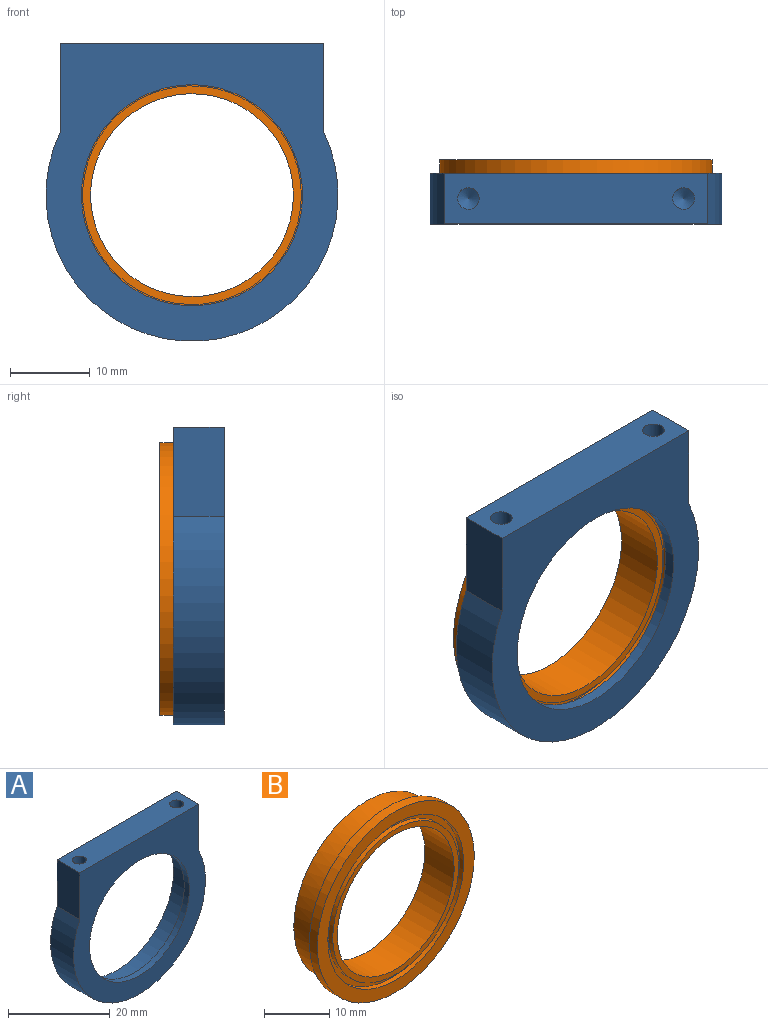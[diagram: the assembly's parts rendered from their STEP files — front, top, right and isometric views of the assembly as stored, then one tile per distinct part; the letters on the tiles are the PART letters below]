
ASSEMBLY  parts=2 mates=1
PART A: 13 faces, bbox 36.6x6.4x37.3 mm
  f0: cylinder r=1.35mm len=7.62mm, axis (0,0,1), area 64.8mm2, adj f1,f7
  f1: cone r=1.35mm half-angle=59deg, axis (0,0,1), area 6.7mm2, adj f0
  f2: cylinder r=1.35mm len=7.62mm, axis (0,0,1), area 64.8mm2, adj f3,f7
  f3: cone r=1.35mm half-angle=59deg, axis (0,0,1), area 6.7mm2, adj f2
  f4: cylinder r=13.84mm len=27.69mm, axis (0,1,0), area 121.5mm2, adj f11,f12
  f5: cylinder r=15.81mm len=31.62mm, axis (0,1,0), area 492.1mm2, adj f10,f12
  f6: cylinder r=18.29mm len=36.58mm, axis (0,-1,0), area 468.1mm2, adj f8,f9,f10,f11
  f7: plane 33.02x6.35mm, normal (0,0,1), area 198.2mm2, adj f0,f2,f8,f9,f10,f11
  f8: plane 11.18x6.35mm, normal (1,0,0), area 71mm2, adj f6,f7,f10,f11
  f9: plane 11.18x6.35mm, normal (-1,0,0), area 71mm2, adj f6,f7,f10,f11
  f10: plane 37.34x36.58mm, normal (0,1,0), area 387.8mm2, adj f5,f6,f7,f8,f9
  f11: plane 37.34x36.58mm, normal (0,-1,0), area 571.2mm2, adj f4,f6,f7,f8,f9
  f12: plane 31.62x31.62mm, normal (0,1,0), area 183.4mm2, adj f4,f5
PART B: 14 faces, bbox 34.1x6.4x34.1 mm
  f0: cylinder r=17.06mm len=34.13mm, axis (0,-1,0), area 183.8mm2, adj f10,f13
  f1: cylinder r=13.69mm len=27.38mm, axis (0,-1,0), area 76.5mm2, adj f7,f12
  f2: cylinder r=14.76mm len=29.52mm, axis (0,-1,0), area 82.4mm2, adj f10,f12
  f3: cylinder r=13.69mm len=27.38mm, axis (0,1,0), area 76.5mm2, adj f8,f11
  f4: cylinder r=14.76mm len=29.52mm, axis (0,1,0), area 82.4mm2, adj f9,f11
  f5: cylinder r=12.7mm len=25.4mm, axis (0,-1,0), area 506.7mm2, adj f7,f8
  f6: cylinder r=15.81mm len=31.62mm, axis (0,-1,0), area 460.5mm2, adj f9,f13
  f7: plane 27.38x27.38mm, normal (0,-1,0), area 82.1mm2, adj f1,f5
  f8: plane 27.38x27.38mm, normal (0,1,0), area 82.1mm2, adj f3,f5
  f9: plane 31.62x31.62mm, normal (0,1,0), area 101.2mm2, adj f4,f6
  f10: plane 34.13x34.13mm, normal (0,-1,0), area 230.4mm2, adj f0,f2
  f11: plane 29.52x29.52mm, normal (0,1,0), area 95.3mm2, adj f3,f4
  f12: plane 29.52x29.52mm, normal (0,-1,0), area 95.3mm2, adj f1,f2
  f13: plane 34.13x34.13mm, normal (0,1,0), area 129.2mm2, adj f0,f6
PLACE A t=(14.13,16.78,27.86)mm
PLACE B rot(axis=(-0.71,0,-0.71),180deg) t=(14.13,24.84,27.86)mm
MATE fastened B.f0 <-> A.f4  axis (0,-1,0) through (14.13,18.49,27.86)mm
